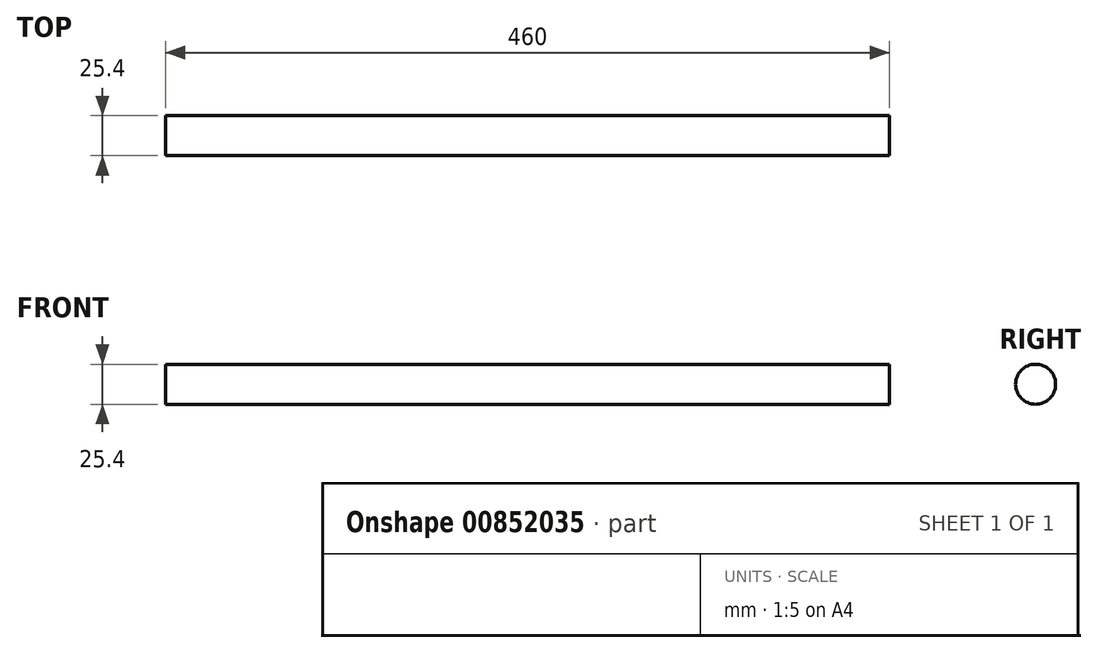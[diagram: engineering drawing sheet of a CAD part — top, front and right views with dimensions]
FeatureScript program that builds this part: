
annotation { "Feature Type Name" : "Feature", "Feature Type Description" : "" }
export const myFeature = defineFeature(function(context is Context, id is Id, definition is map)
    precondition{}
    {
        {
            var Q0;
            Q0=qCreatedBy(makeId("Right.planeOp"),FACE);
            var sketch = newSketch(context, id + "F0", { "sketchPlane" : qUnion([Q0])});
            skCircle(sketch, "E0", {"center": v(0, 0) * mm, "radius": 12.7 * mm});
            skSolve(sketch);
        }
        {
            var Q0;
            Q0=sQuery(id+"F0.wireOp",EDGE,"E0");
            extrude(context, id + "F1", {"bodyType" : ToolBodyType.SURFACE, "surfaceEntities" : qUnion([Q0]), "depth" : 460 * mm, "offsetDistance" : 25.4 * mm});
        }
    });
